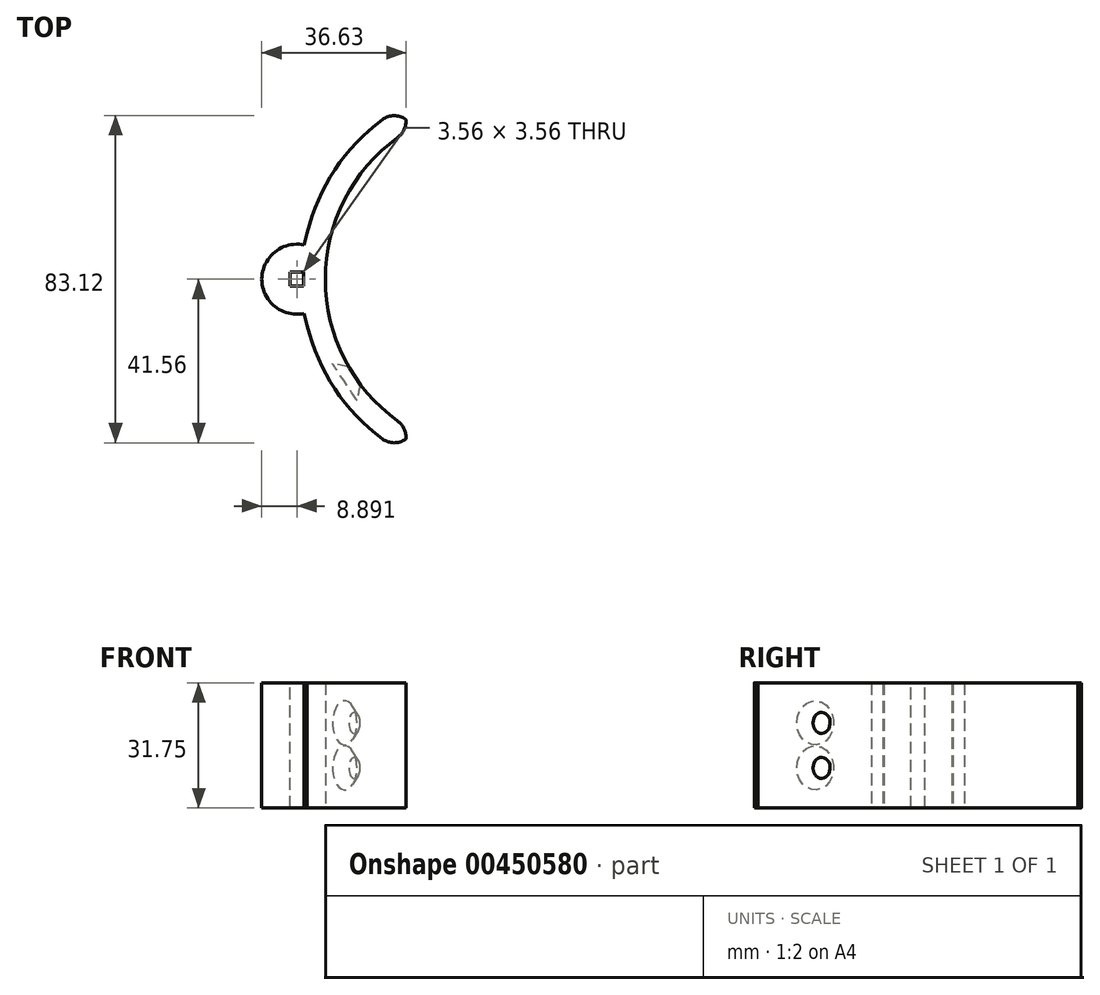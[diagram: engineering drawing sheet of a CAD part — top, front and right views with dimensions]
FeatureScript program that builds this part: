
annotation { "Feature Type Name" : "Feature", "Feature Type Description" : "" }
export const myFeature = defineFeature(function(context is Context, id is Id, definition is map)
    precondition{}
    {
        {
            var Q0;
            Q0=qCreatedBy(makeId("Top.planeOp"),FACE);
            var sketch = newSketch(context, id + "F0", { "sketchPlane" : qUnion([Q0])});
            skArc(sketch, "E0", {"start": v(-22.22, 38.5) * mm, "mid": v(-44.45, 0) * mm, "end": v(-22.22, -38.5) * mm});
            skLineSegment(sketch, "E1", {"start": v(-44.45, 0) * mm, "end": v(-22.23, 0) * mm, "construction": true});
            skPoint(sketch, "E2.start.orphan", {"position": v(-22.23, 0) * mm});
            skArc(sketch, "E3.0", {"start": v(-25.2, 43.66) * mm, "mid": v(-40.4, 30.16) * mm, "end": v(-49.03, 11.75) * mm});
            skLineSegment(sketch, "E4", {"start": v(-25.2, 43.66) * mm, "end": v(-22.22, 38.5) * mm});
            skLineSegment(sketch, "E5", {"start": v(-22.22, -38.5) * mm, "end": v(-25.2, -43.66) * mm});
            skCircle(sketch, "E6", {"center": v(-51.69, 0) * mm, "radius": 1.27 * mm});
            skPoint(sketch, "E6.centerSnap0", {"position": v(-50.42, 0) * mm});
            skLineSegment(sketch, "E7", {"start": v(-49.8, 8.69) * mm, "end": v(-49.03, 11.75) * mm});
            skLineSegment(sketch, "E8", {"start": v(-49.8, -8.69) * mm, "end": v(-49.03, -11.75) * mm});
            skArc(sketch, "E9.trimOffspring", {"start": v(-49.03, -11.75) * mm, "mid": v(-40.4, -30.16) * mm, "end": v(-25.2, -43.66) * mm});
            skArc(sketch, "E10.0", {"start": v(-49.8, 8.69) * mm, "mid": v(-60.58, 0) * mm, "end": v(-49.8, -8.69) * mm});
            skPoint(sketch, "E11.orphan", {"position": v(-51.69, 1.27) * mm});
            skPoint(sketch, "E12.orphan", {"position": v(-51.69, -1.27) * mm});
            skSolve(sketch);
        }
        {
            var Q0;
            Q0=qSketchRegion(id+"F0",true);
            extrude(context, id + "F1", {"entities" : qUnion([Q0]), "depth" : 31.75 * mm});
        }
        {
            var Q0;
            Q0=makeQuery(id+"F1.opExtrude","CAP_FACE",FACE,{"disambiguationData":[OSD([sQuery(id+"F0.wireOp",EDGE,"E0"),sQuery(id+"F0.wireOp",EDGE,"E3.0"),sQuery(id+"F0.wireOp",EDGE,"E4"),sQuery(id+"F0.wireOp",EDGE,"E5"),sQuery(id+"F0.wireOp",EDGE,"E6"),sQuery(id+"F0.wireOp",EDGE,"E7"),sQuery(id+"F0.wireOp",EDGE,"E8"),sQuery(id+"F0.wireOp",EDGE,"E9.trimOffspring"),sQuery(id+"F0.wireOp",EDGE,"E10.0")])],"isStart":false});
            var sketch = newSketch(context, id + "F2", { "sketchPlane" : qUnion([Q0])});
            skLineSegment(sketch, "E13.bottom", {"start": v(-49.91, -1.78) * mm, "end": v(-53.47, -1.78) * mm});
            skLineSegment(sketch, "E13.top", {"start": v(-49.91, 1.78) * mm, "end": v(-53.47, 1.78) * mm});
            skLineSegment(sketch, "E13.left", {"start": v(-49.91, -1.78) * mm, "end": v(-49.91, 1.78) * mm});
            skLineSegment(sketch, "E13.right", {"start": v(-53.47, -1.78) * mm, "end": v(-53.47, 1.78) * mm});
            skPoint(sketch, "E13.middle", {"position": v(-51.69, 0) * mm});
            skSolve(sketch);
        }
        {
            var Q0;
            Q0=makeQuery(id+"F2.imprint","IMPRINT",FACE,{"disambiguationData":[TD([[makeQuery(id+"F2.imprint","IMPRINT",EDGE,{"derivedFrom":sQuery(id+"F2.wireOp",EDGE,"E13.bottom")}),-1.0]])]});
            extrude(context, id + "F3", {"entities" : qUnion([Q0]), "operationType" : NewBodyOperationType.REMOVE, "endBound" : BoundingType.UP_TO_NEXT, "oppositeDirection" : true, "depth" : 25.4 * mm});
        }
        {
            var Q0;
            Q0=makeQuery(id+"F1.opExtrude","SWEPT_EDGE",EDGE,{"disambiguationData":[OSD([sQuery(id+"F0.wireOp",EDGE,"E5"),sQuery(id+"F0.wireOp",EDGE,"E9.trimOffspring")])]});
            var Q1;
            Q1=makeQuery(id+"F1.opExtrude","SWEPT_EDGE",EDGE,{"disambiguationData":[OSD([sQuery(id+"F0.wireOp",EDGE,"E0"),sQuery(id+"F0.wireOp",EDGE,"E5")])]});
            var Q2;
            Q2=makeQuery(id+"F1.opExtrude","SWEPT_EDGE",EDGE,{"disambiguationData":[OSD([sQuery(id+"F0.wireOp",EDGE,"E0"),sQuery(id+"F0.wireOp",EDGE,"E4")])]});
            var Q3;
            Q3=makeQuery(id+"F1.opExtrude","SWEPT_EDGE",EDGE,{"disambiguationData":[OSD([sQuery(id+"F0.wireOp",EDGE,"E3.0"),sQuery(id+"F0.wireOp",EDGE,"E4")])]});
            fillet(context, id + "F4", {"entities" : qUnion([Q0, Q1, Q2, Q3]), "radius" : 5.08 * mm, "tangentPropagation" : true, "allowEdgeOverflow" : false});
        }
        {
            var Q0;
            Q0=makeQuery(id+"F1.opExtrude","CAP_VERTEX",VERTEX,{"disambiguationData":[OSD([sQuery(id+"F0.wireOp",EDGE,"E8"),sQuery(id+"F0.wireOp",EDGE,"E9.trimOffspring")])],"isStart":true});
            var Q1;
            {var subQ0=sQuery(id+"F0.wireOp",EDGE,"E9.trimOffspring");var subQ1=sQuery(id+"F0.wireOp",EDGE,"E5");Q1=makeQuery(id+"F4.opFillet","BLEND_VERTEX",VERTEX,{"blendedFrom":[makeQuery(id+"F1.opExtrude","SWEPT_EDGE",EDGE,{"disambiguationData":[OSD([subQ1,subQ0])]}),makeQuery(id+"F1.opExtrude","SWEPT_FACE",FACE,{"disambiguationData":[OSD([subQ0])]}),makeQuery(id+"F1.opExtrude","CAP_FACE",FACE,{"disambiguationData":[OSD([sQuery(id+"F0.wireOp",EDGE,"E0"),sQuery(id+"F0.wireOp",EDGE,"E3.0"),sQuery(id+"F0.wireOp",EDGE,"E4"),subQ1,sQuery(id+"F0.wireOp",EDGE,"E6"),sQuery(id+"F0.wireOp",EDGE,"E7"),sQuery(id+"F0.wireOp",EDGE,"E8"),subQ0,sQuery(id+"F0.wireOp",EDGE,"E10.0")])],"isStart":false})],"blendedInto":[makeQuery(id+"F1.opExtrude","SWEPT_FACE",FACE,{"disambiguationData":[OSD([subQ0])]}),makeQuery(id+"F1.opExtrude","CAP_FACE",FACE,{"disambiguationData":[OSD([sQuery(id+"F0.wireOp",EDGE,"E0"),sQuery(id+"F0.wireOp",EDGE,"E3.0"),sQuery(id+"F0.wireOp",EDGE,"E4"),subQ1,sQuery(id+"F0.wireOp",EDGE,"E6"),sQuery(id+"F0.wireOp",EDGE,"E7"),sQuery(id+"F0.wireOp",EDGE,"E8"),subQ0,sQuery(id+"F0.wireOp",EDGE,"E10.0")])],"isStart":false})]});}
            var Q2;
            {var subQ0=sQuery(id+"F0.wireOp",EDGE,"E9.trimOffspring");var subQ1=sQuery(id+"F0.wireOp",EDGE,"E5");Q2=makeQuery(id+"F4.opFillet","BLEND_VERTEX",VERTEX,{"blendedFrom":[makeQuery(id+"F1.opExtrude","SWEPT_EDGE",EDGE,{"disambiguationData":[OSD([subQ1,subQ0])]}),makeQuery(id+"F1.opExtrude","SWEPT_FACE",FACE,{"disambiguationData":[OSD([subQ0])]}),makeQuery(id+"F1.opExtrude","CAP_FACE",FACE,{"disambiguationData":[OSD([sQuery(id+"F0.wireOp",EDGE,"E0"),sQuery(id+"F0.wireOp",EDGE,"E3.0"),sQuery(id+"F0.wireOp",EDGE,"E4"),subQ1,sQuery(id+"F0.wireOp",EDGE,"E6"),sQuery(id+"F0.wireOp",EDGE,"E7"),sQuery(id+"F0.wireOp",EDGE,"E8"),subQ0,sQuery(id+"F0.wireOp",EDGE,"E10.0")])],"isStart":true})],"blendedInto":[makeQuery(id+"F1.opExtrude","SWEPT_FACE",FACE,{"disambiguationData":[OSD([subQ0])]}),makeQuery(id+"F1.opExtrude","CAP_FACE",FACE,{"disambiguationData":[OSD([sQuery(id+"F0.wireOp",EDGE,"E0"),sQuery(id+"F0.wireOp",EDGE,"E3.0"),sQuery(id+"F0.wireOp",EDGE,"E4"),subQ1,sQuery(id+"F0.wireOp",EDGE,"E6"),sQuery(id+"F0.wireOp",EDGE,"E7"),sQuery(id+"F0.wireOp",EDGE,"E8"),subQ0,sQuery(id+"F0.wireOp",EDGE,"E10.0")])],"isStart":true})]});}
            cPlane(context, id + "F5", {"entities" : qUnion([Q0, Q1, Q2]), "cplaneType" : CPlaneType.THREE_POINT, "offset" : 25.4 * mm, "width" : 152.4 * mm, "height" : 152.4 * mm});
        }
        {
            var Q0;
            Q0=qCreatedBy(id+"F5.planeOp",FACE);
            var sketch = newSketch(context, id + "F6", { "sketchPlane" : qUnion([Q0])});
            skPoint(sketch, "E14", {"position": v(-8.82, 16.59) * mm});
            skPoint(sketch, "E15", {"position": v(-0.06, 21.59) * mm});
            skPoint(sketch, "E16", {"position": v(-0.06, 10.16) * mm});
            skSolve(sketch);
        }
        {
            var Q0;
            Q0=sQuery(id+"F6.wireOp",VERTEX,"E15");
            var Q1;
            Q1=sQuery(id+"F6.wireOp",VERTEX,"E16");
            var Q2;
            Q2=makeQuery(id+"F1.opExtrude","SWEPT_BODY",BODY,{"disambiguationData":[OSD([sQuery(id+"F0.wireOp",EDGE,"E0"),sQuery(id+"F0.wireOp",EDGE,"E3.0"),sQuery(id+"F0.wireOp",EDGE,"E4"),sQuery(id+"F0.wireOp",EDGE,"E5"),sQuery(id+"F0.wireOp",EDGE,"E6"),sQuery(id+"F0.wireOp",EDGE,"E7"),sQuery(id+"F0.wireOp",EDGE,"E8"),sQuery(id+"F0.wireOp",EDGE,"E9.trimOffspring"),sQuery(id+"F0.wireOp",EDGE,"E10.0")])]});
            hole(context, id + "F7", {"style" : HoleStyle.C_SINK, "endStyle" : HoleEndStyle.THROUGH, "holeDiameter" : 4.83 * mm, "cSinkDiameter" : 11.2 * mm, "cSinkAngle" : 90 * degree, "isTappedThrough" : true, "tappedDepth" : 12.7 * mm, "tapClearance" : 3, "locations" : qUnion([Q0, Q1]), "scope" : qUnion([Q2])});
        }
    });
